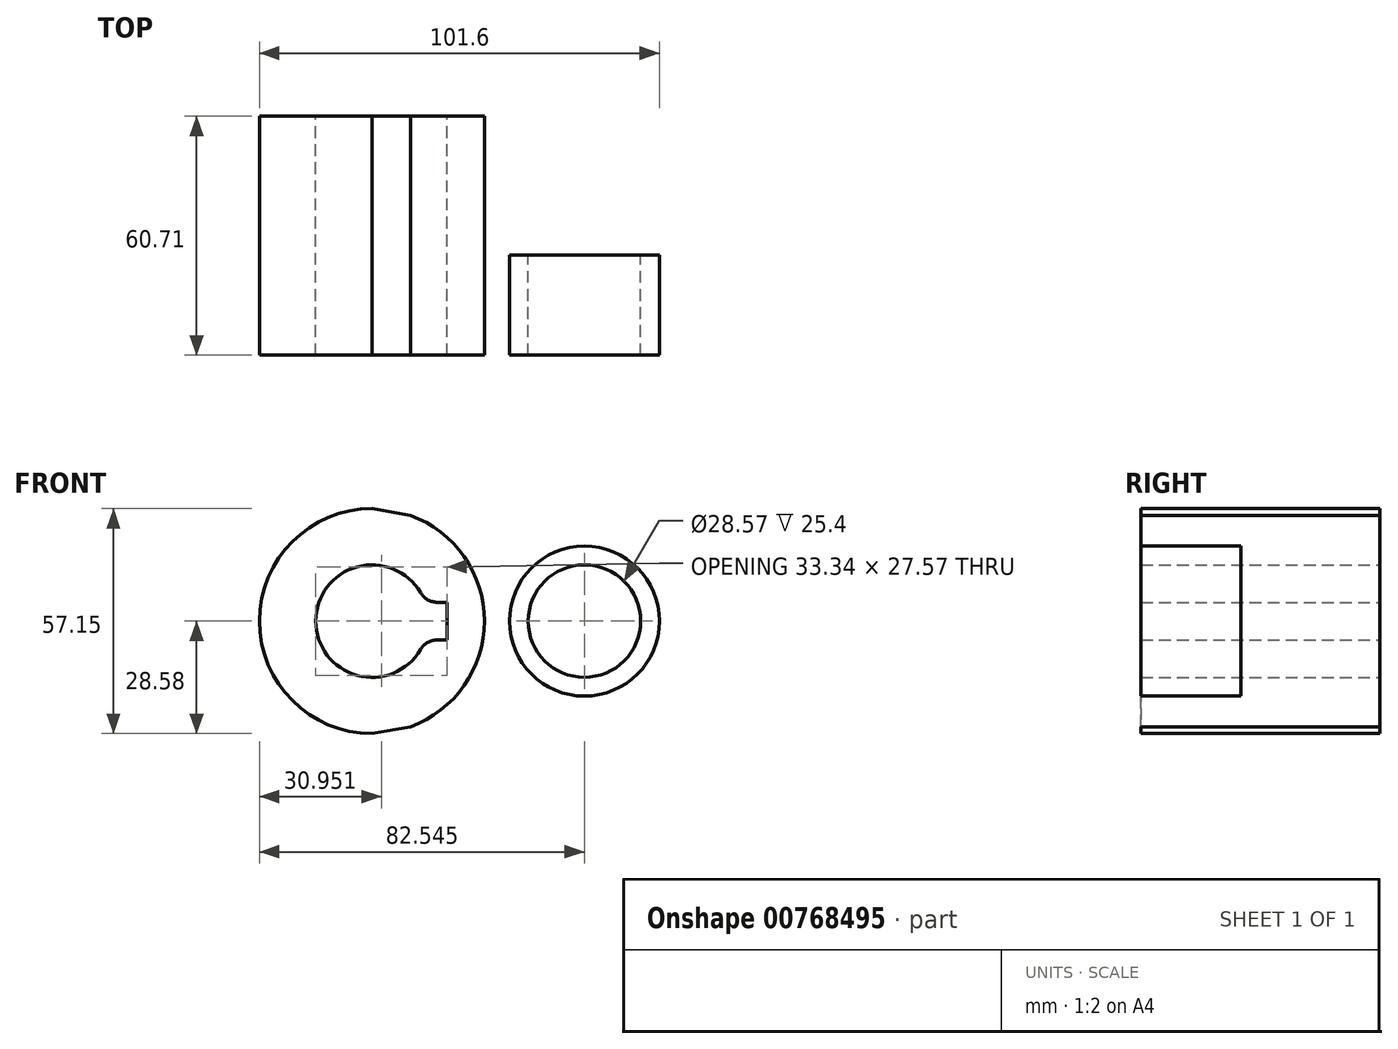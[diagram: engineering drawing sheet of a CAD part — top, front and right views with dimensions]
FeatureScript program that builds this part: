
annotation { "Feature Type Name" : "Feature", "Feature Type Description" : "" }
export const myFeature = defineFeature(function(context is Context, id is Id, definition is map)
    precondition{}
    {
        {
            var Q0;
            Q0=qCreatedBy(makeId("Front.planeOp"),FACE);
            var sketch = newSketch(context, id + "F0", { "sketchPlane" : qUnion([Q0])});
            skCircle(sketch, "E0", {"center": v(0, 0) * mm, "radius": 28.58 * mm});
            skCircle(sketch, "E1", {"center": v(53.98, 0) * mm, "radius": 19.05 * mm});
            skLineSegment(sketch, "E2", {"start": v(0, -28.58) * mm, "end": v(53.95, -19.05) * mm});
            skCircle(sketch, "E3", {"center": v(0, 0) * mm, "radius": 14.29 * mm});
            skCircle(sketch, "E4", {"center": v(53.98, 0) * mm, "radius": 14.29 * mm});
            skLineSegment(sketch, "E5.bottom", {"start": v(19.05, 4.76) * mm, "end": v(-19.05, 4.76) * mm});
            skLineSegment(sketch, "E5.top", {"start": v(19.05, -4.76) * mm, "end": v(-19.05, -4.76) * mm});
            skLineSegment(sketch, "E5.left", {"start": v(19.05, 4.76) * mm, "end": v(19.05, -4.76) * mm});
            skLineSegment(sketch, "E5.right", {"start": v(-19.05, 4.76) * mm, "end": v(-19.05, -4.76) * mm});
            skLineSegment(sketch, "E6", {"start": v(0, 28.58) * mm, "end": v(53.97, 19.05) * mm});
            skSolve(sketch);
        }
        {
            var Q0;
            {var subQ4=sQuery(id+"F0.wireOp",EDGE,"E5.left");Q0=makeQuery(id+"F0.imprint","IMPRINT",FACE,{"disambiguationData":[TD([[makeQuery(id+"F0.imprint","IMPRINT",EDGE,{"derivedFrom":subQ4}),1.0]])]});}
            var Q1;
            {var subQ0=sQuery(id+"F0.wireOp",EDGE,"E6");var subQ1=sQuery(id+"F0.wireOp",EDGE,"E0");var subQ2=makeQuery(id+"F0.imprint","INTERSECT",VERTEX,{"disambiguationData":[OD(1.0)],"derivedFrom":[subQ1,subQ0]});Q1=makeQuery(id+"F0.imprint","IMPRINT",FACE,{"disambiguationData":[TD([[makeQuery(id+"F0.imprint","IMPRINT",EDGE,{"disambiguationData":[TD([[subQ2,1.0]])],"derivedFrom":subQ1}),-1.0]])]});}
            var Q2;
            Q2=makeQuery(id+"F0.imprint","IMPRINT",FACE,{"disambiguationData":[TD([[makeQuery(id+"F0.imprint","IMPRINT",EDGE,{"derivedFrom":sQuery(id+"F0.wireOp",EDGE,"E4")}),-1.0]])]});
            var Q3;
            {var subQ5=sQuery(id+"F0.wireOp",EDGE,"E5.right");Q3=makeQuery(id+"F0.imprint","IMPRINT",FACE,{"disambiguationData":[TD([[makeQuery(id+"F0.imprint","IMPRINT",EDGE,{"derivedFrom":subQ5}),1.0]])]});}
            extrude(context, id + "F1", {"entities" : qUnion([Q0, Q1, Q2, Q3]), "depth" : 25.4 * mm, "offsetDistance" : 25.4 * mm});
        }
        {
            var Q0;
            {var subQ4=sQuery(id+"F0.wireOp",EDGE,"E5.left");Q0=makeQuery(id+"F0.imprint","IMPRINT",FACE,{"disambiguationData":[TD([[makeQuery(id+"F0.imprint","IMPRINT",EDGE,{"derivedFrom":subQ4}),1.0]])]});}
            var Q1;
            {var subQ5=sQuery(id+"F0.wireOp",EDGE,"E5.right");Q1=makeQuery(id+"F0.imprint","IMPRINT",FACE,{"disambiguationData":[TD([[makeQuery(id+"F0.imprint","IMPRINT",EDGE,{"derivedFrom":subQ5}),1.0]])]});}
            extrude(context, id + "F2", {"entities" : qUnion([Q0, Q1]), "operationType" : NewBodyOperationType.ADD, "oppositeDirection" : true, "depth" : 35.3 * mm, "offsetDistance" : 25.4 * mm});
        }
        {
            var Q0;
            {var subQ0=sQuery(id+"F0.wireOp",EDGE,"E5.top");var subQ1=sQuery(id+"F0.wireOp",EDGE,"E3");Q0=makeQuery(id+"F2.boolean.opBoolean","MERGE",EDGE,{"derivedFrom":[makeQuery(id+"F1.opExtrude","SWEPT_EDGE",EDGE,{"disambiguationData":[OSD([subQ1,subQ0])]}),makeQuery(id+"F2.opExtrude","SWEPT_EDGE",EDGE,{"disambiguationData":[OSD([subQ1,subQ0])]})]});}
            var Q1;
            {var subQ0=sQuery(id+"F0.wireOp",EDGE,"E5.bottom");var subQ1=sQuery(id+"F0.wireOp",EDGE,"E3");Q1=makeQuery(id+"F2.boolean.opBoolean","MERGE",EDGE,{"derivedFrom":[makeQuery(id+"F1.opExtrude","SWEPT_EDGE",EDGE,{"disambiguationData":[OSD([subQ1,subQ0])]}),makeQuery(id+"F2.opExtrude","SWEPT_EDGE",EDGE,{"disambiguationData":[OSD([subQ1,subQ0])]})]});}
            fillet(context, id + "F3", {"entities" : qUnion([Q0, Q1]), "radius" : 5.08 * mm, "tangentPropagation" : true, "allowEdgeOverflow" : false});
        }
    });
